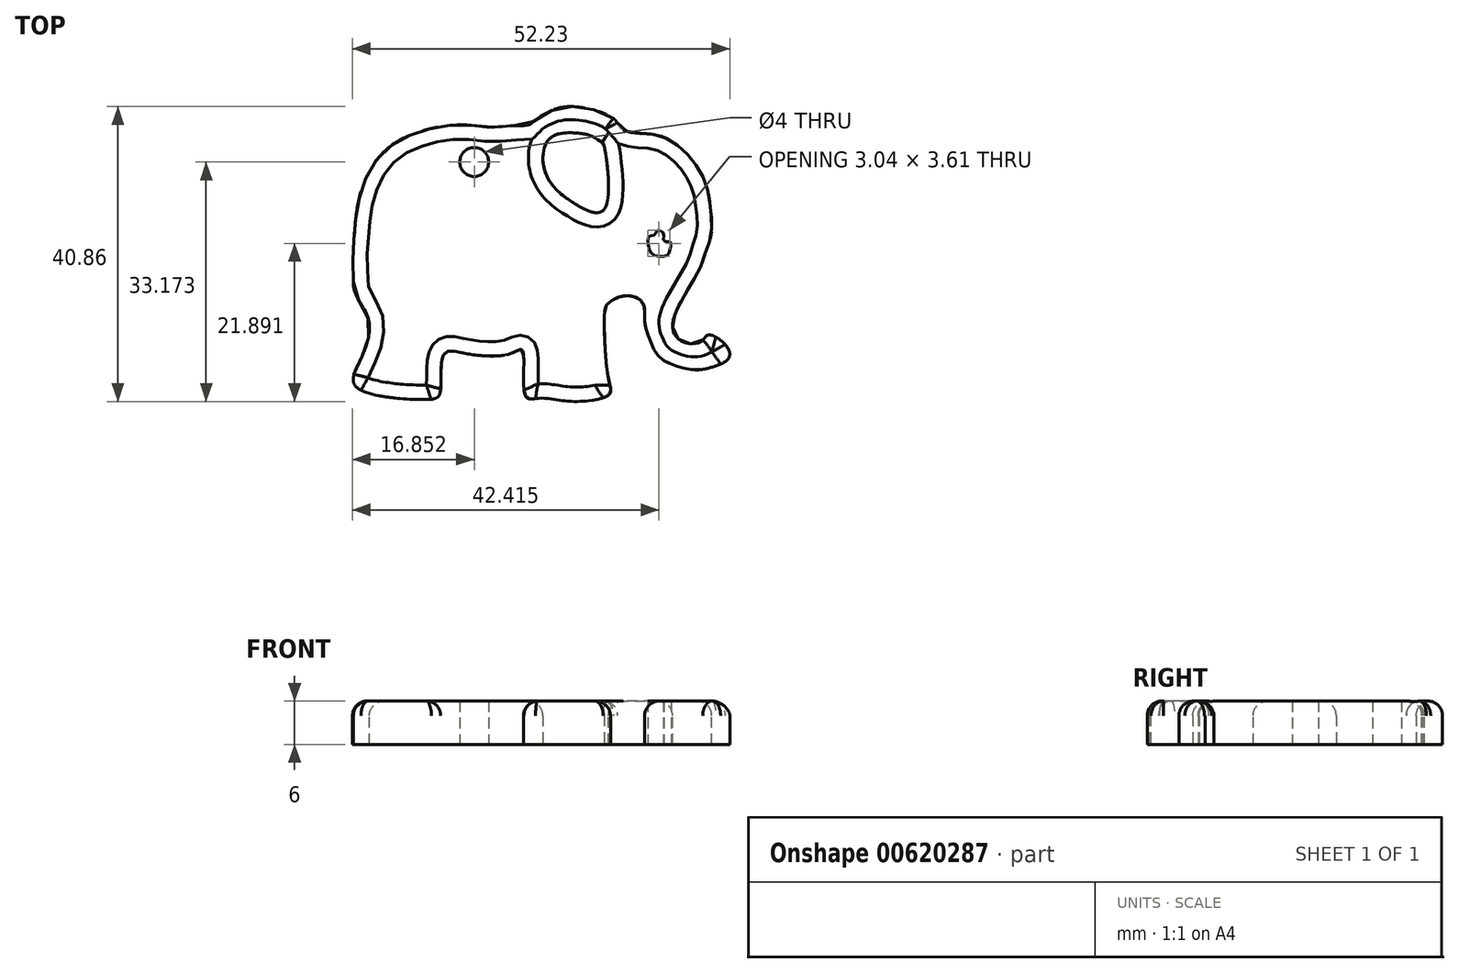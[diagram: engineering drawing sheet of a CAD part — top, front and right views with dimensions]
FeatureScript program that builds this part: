
annotation { "Feature Type Name" : "Feature", "Feature Type Description" : "" }
export const myFeature = defineFeature(function(context is Context, id is Id, definition is map)
    precondition{}
    {
        {
            var Q0;
            Q0=qCreatedBy(makeId("Top.planeOp"),FACE);
            var sketch = newSketch(context, id + "F0", { "sketchPlane" : qUnion([Q0])});
            skFitSpline(sketch, "E0", {"points": [v(40.8, 28.81) * mm, v(40.67, 37.72) * mm, v(40.47, 37.98) * mm, v(39.2, 38.78) * mm, v(36.55, 39.31) * mm, v(33.75, 38.91) * mm, v(32.36, 36.92) * mm, v(32.96, 33) * mm, v(36.81, 29.41) * mm, v(40.8, 28.81) * mm]});
            skFitSpline(sketch, "E1", {"points": [v(49.84, 23.1) * mm, v(49.37, 22.3) * mm, v(47.64, 22.37) * mm, v(46.85, 23.63) * mm, v(47.04, 25.03) * mm, v(47.7, 25.16) * mm, v(48.1, 25.76) * mm, v(48.97, 25.42) * mm, v(48.97, 24.36) * mm, v(49.9, 24.16) * mm, v(49.84, 23.1) * mm]});
            skFitSpline(sketch, "E2", {"points": [v(40.8, 14.46) * mm, v(41.26, 15.66) * mm, v(43.39, 16.72) * mm, v(46.05, 15.86) * mm, v(46.38, 12.93) * mm, v(47.31, 10.07) * mm, v(47.97, 8.68) * mm, v(49.84, 7.35) * mm, v(53.42, 6.49) * mm, v(55.95, 6.95) * mm, v(57.88, 7.95) * mm, v(58, 9.21) * mm, v(56.35, 10.94) * mm, v(55.02, 11.27) * mm, v(54.22, 10.47) * mm, v(52.3, 10.14) * mm, v(50.43, 11.47) * mm, v(50.43, 13.86) * mm, v(52.1, 17.19) * mm, v(54.15, 20.9) * mm, v(54.89, 23.1) * mm, v(55.55, 25.23) * mm, v(55.48, 28.81) * mm, v(54.75, 32.34) * mm, v(52.56, 36) * mm, v(48.77, 38.78) * mm, v(45.05, 39.31) * mm, v(43, 39.98) * mm, v(42.2, 41.17) * mm, v(37.67, 42.83) * mm, v(34.82, 42.83) * mm, v(33.42, 42.37) * mm, v(31.23, 41.17) * mm, v(30.37, 40.44) * mm, v(28.3, 40.3) * mm, v(24.92, 40.11) * mm, v(21, 40.44) * mm, v(14.68, 39.31) * mm, v(9.77, 36.19) * mm, v(6.78, 30.08) * mm, v(6.11, 24.76) * mm, v(5.91, 23.1) * mm, v(5.98, 20.57) * mm, v(6.31, 17.05) * mm, v(8.1, 13.53) * mm, v(7.24, 8.41) * mm, v(6.38, 4.16) * mm, v(15.81, 2.37) * mm, v(17.27, 2.5) * mm, v(18, 3.23) * mm, v(18.54, 8.68) * mm, v(21.26, 8.81) * mm, v(27.84, 8.75) * mm, v(29.44, 9.14) * mm, v(29.83, 2.9) * mm, v(31.16, 2.5) * mm, v(33.16, 2.5) * mm, v(36.55, 2.1) * mm, v(41.4, 3.03) * mm, v(41.33, 5.22) * mm, v(40.8, 14.46) * mm]});
            skCircle(sketch, "E3", {"center": v(22.75, 35.27) * mm, "radius": 2 * mm});
            skSolve(sketch);
        }
        {
            var Q0;
            Q0 = qSketchRegion(id + "F0", true);
            extrude(context, id + "F1", {"entities" : qUnion([Q0]), "depth" : 6 * mm, "offsetDistance" : 25 * mm});
        }
        {
            var Q0;
            Q0=makeQuery(id+"F1.opExtrude","CAP_EDGE",EDGE,{"disambiguationData":[OSD([sQuery(id+"F0.wireOp",EDGE,"E2")])],"isStart":false});
            var Q1;
            Q1=makeQuery(id+"F1.opExtrude","CAP_EDGE",EDGE,{"disambiguationData":[OSD([sQuery(id+"F0.wireOp",EDGE,"E0")])],"isStart":false});
            fillet(context, id + "F2", {"entities" : qUnion([Q0, Q1]), "radius" : 2 * mm, "allowEdgeOverflow" : false});
        }
    });
